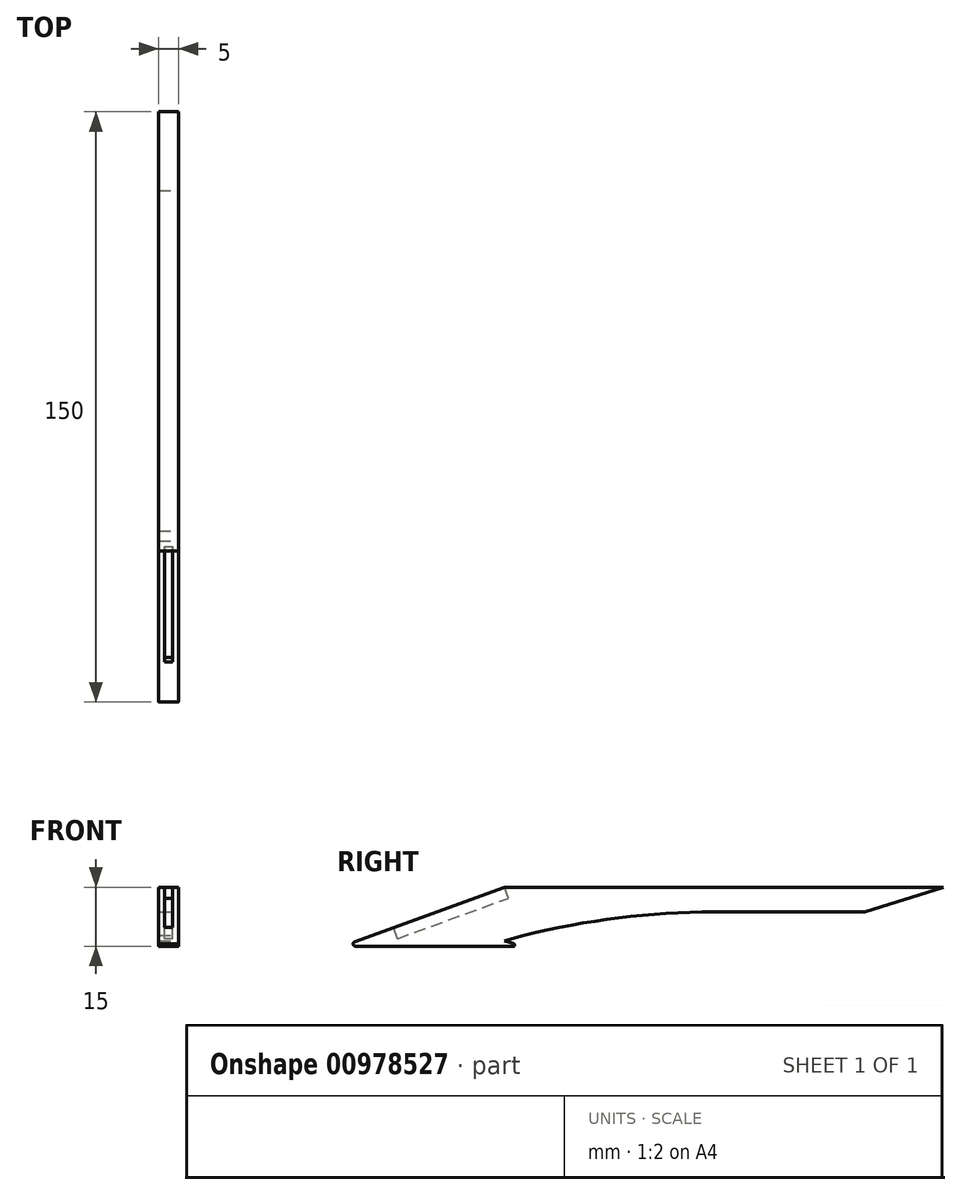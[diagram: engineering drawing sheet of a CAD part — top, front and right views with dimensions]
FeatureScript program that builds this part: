
annotation { "Feature Type Name" : "Feature", "Feature Type Description" : "" }
export const myFeature = defineFeature(function(context is Context, id is Id, definition is map)
    precondition{}
    {
        {
            var Q0;
            Q0=qCreatedBy(makeId("Top.planeOp"),FACE);
            var sketch = newSketch(context, id + "F0", { "sketchPlane" : qUnion([Q0])});
            skLineSegment(sketch, "E0", {"start": v(0, 0) * mm, "end": v(0, -75) * mm, "construction": true});
            skLineSegment(sketch, "E1", {"start": v(0, 0) * mm, "end": v(0, 75) * mm, "construction": true});
            skLineSegment(sketch, "E2", {"start": v(0, 75) * mm, "end": v(2.5, 75) * mm, "construction": true});
            skLineSegment(sketch, "E3", {"start": v(0, -75) * mm, "end": v(-2.5, -75) * mm, "construction": true});
            skLineSegment(sketch, "E4.bottom", {"start": v(2.5, 75) * mm, "end": v(-2.5, 75) * mm});
            skLineSegment(sketch, "E4.top", {"start": v(2.5, -75) * mm, "end": v(-2.5, -75) * mm});
            skLineSegment(sketch, "E4.left", {"start": v(2.5, 75) * mm, "end": v(2.5, -75) * mm});
            skLineSegment(sketch, "E4.right", {"start": v(-2.5, 75) * mm, "end": v(-2.5, -75) * mm});
            skSolve(sketch);
        }
        {
            var Q0;
            Q0=makeQuery(id+"F0.imprint","IMPRINT",FACE,{"disambiguationData":[TD([[makeQuery(id+"F0.imprint","IMPRINT",EDGE,{"derivedFrom":sQuery(id+"F0.wireOp",EDGE,"E4.bottom")}),1.0]])]});
            extrude(context, id + "F1", {"entities" : qUnion([Q0]), "depth" : 15 * mm, "offsetDistance" : 25 * mm});
        }
        {
            var Q0;
            Q0=makeQuery(id+"F1.opExtrude","CAP_EDGE",EDGE,{"disambiguationData":[OSD([sQuery(id+"F0.wireOp",EDGE,"E4.top")])],"isStart":false});
            chamfer(context, id + "F2", {"entities" : qUnion([Q0]), "chamferType" : ChamferType.OFFSET_ANGLE, "width" : 14 * mm, "oppositeDirection" : false, "angle" : 70 * degree, "tangentPropagation" : true});
        }
        {
            var Q0;
            {var subQ0=sQuery(id+"F0.wireOp",EDGE,"E4.top");Q0=makeQuery(id+"F2.opChamfer","BLEND_EDGE",EDGE,{"blendedFrom":[makeQuery(id+"F1.opExtrude","CAP_EDGE",EDGE,{"disambiguationData":[OSD([subQ0])],"isStart":false}),makeQuery(id+"F1.opExtrude","SWEPT_FACE",FACE,{"disambiguationData":[OSD([subQ0])]})],"blendedInto":[makeQuery(id+"F1.opExtrude","SWEPT_FACE",FACE,{"disambiguationData":[OSD([subQ0])]})]});}
            var Q1;
            Q1=makeQuery(id+"F1.opExtrude","CAP_EDGE",EDGE,{"disambiguationData":[OSD([sQuery(id+"F0.wireOp",EDGE,"E4.top")])],"isStart":true});
            fillet(context, id + "F3", {"entities" : qUnion([Q0, Q1]), "radius" : 0.6 * mm, "tangentPropagation" : true, "allowEdgeOverflow" : false});
        }
        {
            var Q0;
            Q0=makeQuery(id+"F1.opExtrude","SWEPT_FACE",FACE,{"disambiguationData":[OSD([sQuery(id+"F0.wireOp",EDGE,"E4.left")])]});
            var sketch = newSketch(context, id + "F4", { "sketchPlane" : qUnion([Q0])});
            skLineSegment(sketch, "E5", {"start": v(-36.54, 0) * mm, "end": v(-41.54, 0) * mm, "construction": true});
            skArc(sketch, "E6", {"start": v(75, 0) * mm, "mid": v(16.73, 8.68) * mm, "end": v(-41.54, 0) * mm});
            skLineSegment(sketch, "E7", {"start": v(75, 8.68) * mm, "end": v(55, 8.68) * mm, "construction": true});
            skLineSegment(sketch, "E8", {"start": v(55, 8.68) * mm, "end": v(75, 15) * mm});
            skLineSegment(sketch, "E9", {"start": v(16.73, 8.68) * mm, "end": v(75, 8.68) * mm});
            skLineSegment(sketch, "E10", {"start": v(-36.54, 15) * mm, "end": v(-31.54, 15) * mm, "construction": true});
            skLineSegment(sketch, "E11", {"start": v(-31.54, 15) * mm, "end": v(-31.54, 0) * mm});
            skLineSegment(sketch, "E12", {"start": v(-31.54, 0) * mm, "end": v(-31.54, 2.76) * mm, "construction": true});
            skLineSegment(sketch, "E13", {"start": v(-31.54, 2.76) * mm, "end": v(-36.54, 1.38) * mm});
            skLineSegment(sketch, "E14", {"start": v(-36.54, 1.38) * mm, "end": v(-31.54, 0) * mm});
            skLineSegment(sketch, "E15", {"start": v(-34.04, 0.7) * mm, "end": v(-34.04, 0) * mm});
            skSolve(sketch);
        }
        {
            var Q0;
            {var subQ4=sQuery(id+"F4.wireOp",EDGE,"E8");Q0=makeQuery(id+"F4.imprint","IMPRINT",FACE,{"disambiguationData":[TD([[makeQuery(id+"F4.imprint","IMPRINT",EDGE,{"derivedFrom":subQ4}),-1.0]])]});}
            var Q1;
            {var subQ4=sQuery(id+"F4.wireOp",EDGE,"E9");var subQ6=makeQuery(id+"F4.imprint","INTERSECT",VERTEX,{"derivedFrom":[sQuery(id+"F4.wireOp",EDGE,"E8"),subQ4]});Q1=makeQuery(id+"F4.imprint","IMPRINT",FACE,{"disambiguationData":[TD([[makeQuery(id+"F4.imprint","IMPRINT",EDGE,{"disambiguationData":[TD([[subQ6,1.0]])],"derivedFrom":subQ4}),-1.0]])]});}
            var Q2;
            {var subQ0=sQuery(id+"F4.wireOp",EDGE,"E6");var subQ4=makeQuery(id+"F4.imprint","INTERSECT",VERTEX,{"derivedFrom":[subQ0,sQuery(id+"F4.wireOp",EDGE,"E9")]});Q2=makeQuery(id+"F4.imprint","IMPRINT",FACE,{"disambiguationData":[TD([[makeQuery(id+"F4.imprint","IMPRINT",EDGE,{"disambiguationData":[TD([[subQ4,-1.0]])],"derivedFrom":subQ0}),1.0]])]});}
            var Q3;
            {var subQ2=sQuery(id+"F4.wireOp",EDGE,"E13");Q3=makeQuery(id+"F4.imprint","IMPRINT",FACE,{"disambiguationData":[TD([[makeQuery(id+"F4.imprint","IMPRINT",EDGE,{"derivedFrom":subQ2}),1.0]])]});}
            var Q4;
            {var subQ3=sQuery(id+"F4.wireOp",EDGE,"E15");Q4=makeQuery(id+"F4.imprint","IMPRINT",FACE,{"disambiguationData":[TD([[makeQuery(id+"F4.imprint","IMPRINT",EDGE,{"derivedFrom":subQ3}),1.0]])]});}
            extrude(context, id + "F5", {"entities" : qUnion([Q0, Q1, Q2, Q3, Q4]), "operationType" : NewBodyOperationType.REMOVE, "oppositeDirection" : true, "depth" : 25 * mm, "offsetDistance" : 25 * mm});
        }
        {
            var Q0;
            Q0=makeQuery(id+"F5.boolean.opBoolean","COPY",EDGE,{"derivedFrom":makeQuery(id+"F5.opExtrude","SWEPT_EDGE",EDGE,{"disambiguationData":[OSD([sQuery(id+"F4.wireOp",EDGE,"E14"),sQuery(id+"F4.wireOp",EDGE,"E15")])]})});
            var Q1;
            Q1=makeQuery(id+"F5.boolean.opBoolean","COPY",EDGE,{"derivedFrom":makeQuery(id+"F5.opExtrude","SWEPT_EDGE",EDGE,{"disambiguationData":[OSD([sQuery(id+"F0.wireOp",EDGE,"E4.left"),sQuery(id+"F4.wireOp",EDGE,"E15")])]})});
            fillet(context, id + "F6", {"entities" : qUnion([Q0, Q1]), "radius" : 0.4 * mm, "tangentPropagation" : true, "allowEdgeOverflow" : false});
        }
        {
            var Q0;
            Q0=makeQuery(id+"F2.opChamfer","BLEND_FACE",FACE,{"disambiguationData":[OSD([sQuery(id+"F0.wireOp",EDGE,"E4.top")])]});
            var sketch = newSketch(context, id + "F7", { "sketchPlane" : qUnion([Q0])});
            skLineSegment(sketch, "E16", {"start": v(-2.5, -29.2) * mm, "end": v(2.5, -29.2) * mm});
            skLineSegment(sketch, "E17", {"start": v(2.5, -29.2) * mm, "end": v(1, -29.2) * mm});
            skLineSegment(sketch, "E18", {"start": v(1, -29.2) * mm, "end": v(-1, -29.2) * mm});
            skLineSegment(sketch, "E19", {"start": v(-1, -29.2) * mm, "end": v(-2.5, -29.2) * mm});
            skLineSegment(sketch, "E20", {"start": v(1, -29.2) * mm, "end": v(1, -59.2) * mm, "construction": true});
            skLineSegment(sketch, "E21.bottom", {"start": v(1, -59.2) * mm, "end": v(-1, -59.2) * mm});
            skLineSegment(sketch, "E21.left", {"start": v(1, -59.2) * mm, "end": v(1, -29.2) * mm});
            skLineSegment(sketch, "E21.right", {"start": v(-1, -59.2) * mm, "end": v(-1, -29.2) * mm});
            skSolve(sketch);
        }
        {
            var Q0;
            Q0=makeQuery(id+"F7.imprint","IMPRINT",FACE,{"disambiguationData":[TD([[makeQuery(id+"F7.imprint","IMPRINT",EDGE,{"derivedFrom":sQuery(id+"F7.wireOp",EDGE,"E21.bottom")}),-1.0]])]});
            extrude(context, id + "F8", {"entities" : qUnion([Q0]), "operationType" : NewBodyOperationType.REMOVE, "oppositeDirection" : true, "depth" : 3 * mm, "offsetDistance" : 25 * mm});
        }
    });
